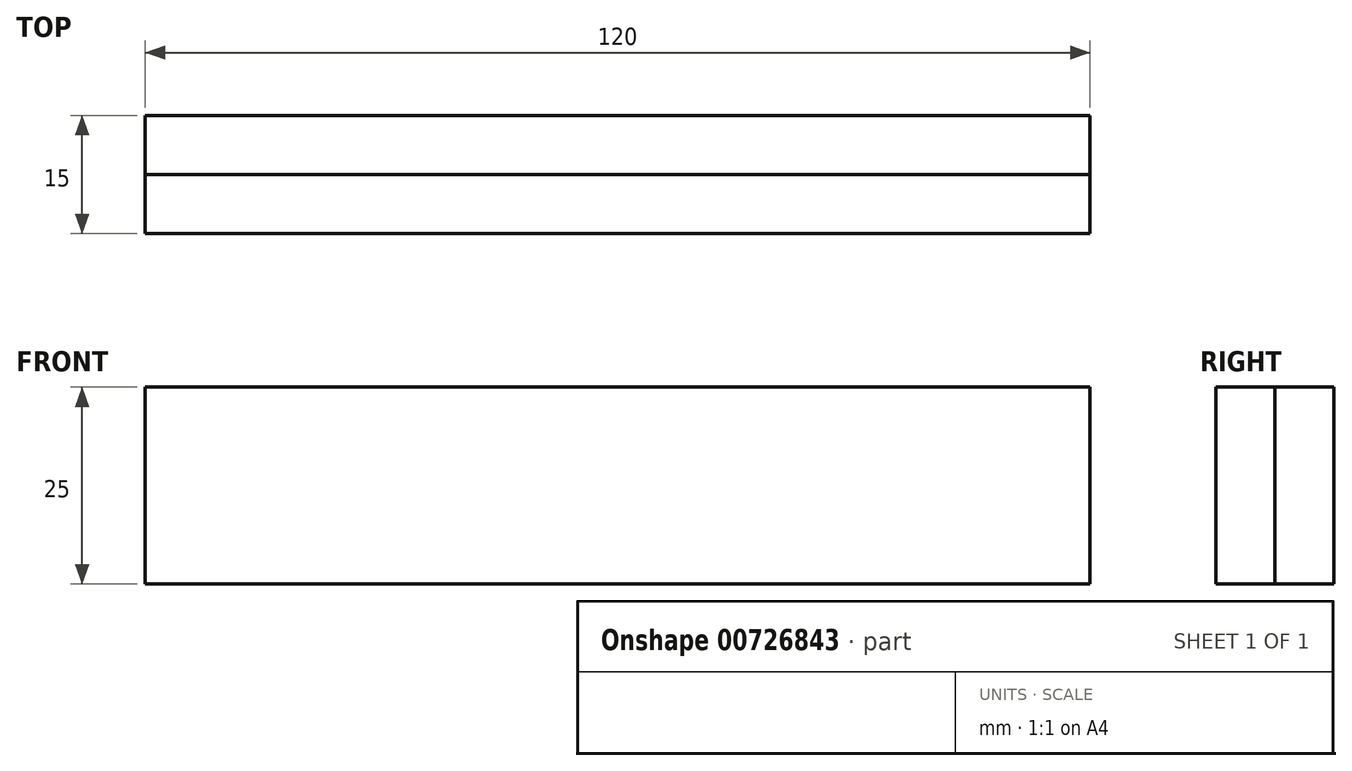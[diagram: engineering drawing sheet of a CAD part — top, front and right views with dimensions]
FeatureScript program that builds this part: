
annotation { "Feature Type Name" : "Feature", "Feature Type Description" : "" }
export const myFeature = defineFeature(function(context is Context, id is Id, definition is map)
    precondition{}
    {
        {
            var Q0;
            Q0=qCreatedBy(makeId("Top.planeOp"),FACE);
            var sketch = newSketch(context, id + "F0", { "sketchPlane" : qUnion([Q0])});
            skLineSegment(sketch, "E0.bottom", {"start": v(-60.51, -1.27) * mm, "end": v(-50.51, -1.27) * mm});
            skLineSegment(sketch, "E0.top", {"start": v(-60.51, -11.27) * mm, "end": v(-50.51, -11.27) * mm});
            skLineSegment(sketch, "E0.left", {"start": v(-60.51, -1.27) * mm, "end": v(-60.51, -11.27) * mm});
            skLineSegment(sketch, "E0.right", {"start": v(-50.51, -1.27) * mm, "end": v(-50.51, -11.27) * mm});
            skCircle(sketch, "E1", {"center": v(-55.51, -6.27) * mm, "radius": 5 * mm});
            skPoint(sketch, "E1.centerSnap0", {"position": v(-55.51, -11.27) * mm});
            skPoint(sketch, "E1.centerSnap1", {"position": v(-60.51, -6.27) * mm});
            skLineSegment(sketch, "E2.bottom", {"start": v(-40.9, 0.93) * mm, "end": v(79.1, 0.93) * mm});
            skLineSegment(sketch, "E2.top", {"start": v(-40.9, -14.07) * mm, "end": v(79.1, -14.07) * mm});
            skLineSegment(sketch, "E2.left", {"start": v(-40.9, 0.93) * mm, "end": v(-40.9, -14.07) * mm});
            skLineSegment(sketch, "E2.right", {"start": v(79.1, 0.93) * mm, "end": v(79.1, -14.07) * mm});
            skLineSegment(sketch, "E3", {"start": v(-40.9, -6.57) * mm, "end": v(79.1, -6.57) * mm});
            skSolve(sketch);
        }
        {
            var Q0;
            {var subQ0=sQuery(id+"F0.wireOp",EDGE,"E0.left");var subQ1=sQuery(id+"F0.wireOp",EDGE,"E0.bottom");var subQ2=makeQuery(id+"F0.imprint","INTERSECT",VERTEX,{"derivedFrom":[subQ1,subQ0]});Q0=makeQuery(id+"F0.imprint","IMPRINT",FACE,{"disambiguationData":[TD([[makeQuery(id+"F0.imprint","IMPRINT",EDGE,{"disambiguationData":[TD([[subQ2,-1.0]])],"derivedFrom":subQ1}),-1.0]])]});}
            var Q1;
            {var subQ0=sQuery(id+"F0.wireOp",EDGE,"E0.right");var subQ1=sQuery(id+"F0.wireOp",EDGE,"E0.bottom");var subQ2=makeQuery(id+"F0.imprint","INTERSECT",VERTEX,{"derivedFrom":[subQ1,subQ0]});Q1=makeQuery(id+"F0.imprint","IMPRINT",FACE,{"disambiguationData":[TD([[makeQuery(id+"F0.imprint","IMPRINT",EDGE,{"disambiguationData":[TD([[subQ2,1.0]])],"derivedFrom":subQ1}),-1.0]])]});}
            var Q2;
            {var subQ0=sQuery(id+"F0.wireOp",EDGE,"E0.left");var subQ1=sQuery(id+"F0.wireOp",EDGE,"E0.top");var subQ2=makeQuery(id+"F0.imprint","INTERSECT",VERTEX,{"derivedFrom":[subQ1,subQ0]});Q2=makeQuery(id+"F0.imprint","IMPRINT",FACE,{"disambiguationData":[TD([[makeQuery(id+"F0.imprint","IMPRINT",EDGE,{"disambiguationData":[TD([[subQ2,-1.0]])],"derivedFrom":subQ1}),1.0]])]});}
            var Q3;
            {var subQ0=sQuery(id+"F0.wireOp",EDGE,"E0.right");var subQ1=sQuery(id+"F0.wireOp",EDGE,"E0.top");var subQ2=makeQuery(id+"F0.imprint","INTERSECT",VERTEX,{"derivedFrom":[subQ1,subQ0]});Q3=makeQuery(id+"F0.imprint","IMPRINT",FACE,{"disambiguationData":[TD([[makeQuery(id+"F0.imprint","IMPRINT",EDGE,{"disambiguationData":[TD([[subQ2,1.0]])],"derivedFrom":subQ1}),1.0]])]});}
            var Q4;
            {var subQ0=sQuery(id+"F0.wireOp",EDGE,"E2.top");Q4=makeQuery(id+"F0.imprint","IMPRINT",FACE,{"disambiguationData":[TD([[makeQuery(id+"F0.imprint","IMPRINT",EDGE,{"derivedFrom":subQ0}),1.0]])]});}
            extrude(context, id + "F1", {"entities" : qUnion([Q0, Q1, Q2, Q3, Q4]), "depth" : 25 * mm, "offsetDistance" : 25 * mm});
        }
        {
            var Q0;
            {var subQ0=sQuery(id+"F0.wireOp",EDGE,"E1");var subQ1=makeQuery(id+"F0.imprint","INTERSECT",VERTEX,{"derivedFrom":[sQuery(id+"F0.wireOp",EDGE,"E0.bottom"),subQ0]});Q0=makeQuery(id+"F0.imprint","IMPRINT",FACE,{"disambiguationData":[TD([[makeQuery(id+"F0.imprint","IMPRINT",EDGE,{"disambiguationData":[TD([[subQ1,1.0]])],"derivedFrom":subQ0}),1.0]])]});}
            var Q1;
            {var subQ0=sQuery(id+"F0.wireOp",EDGE,"E2.bottom");Q1=makeQuery(id+"F0.imprint","IMPRINT",FACE,{"disambiguationData":[TD([[makeQuery(id+"F0.imprint","IMPRINT",EDGE,{"derivedFrom":subQ0}),-1.0]])]});}
            extrude(context, id + "F2", {"entities" : qUnion([Q0, Q1]), "depth" : 25 * mm, "offsetDistance" : 25 * mm});
        }
        {
            var Q0;
            Q0=makeQuery(id+"F1.opExtrude","SWEPT_BODY",BODY,{"disambiguationData":[OSD([sQuery(id+"F0.wireOp",EDGE,"E0.top"),sQuery(id+"F0.wireOp",EDGE,"E0.right"),sQuery(id+"F0.wireOp",EDGE,"E1")])]});
            var Q1;
            Q1=makeQuery(id+"F1.opExtrude","SWEPT_BODY",BODY,{"disambiguationData":[OSD([sQuery(id+"F0.wireOp",EDGE,"E0.bottom"),sQuery(id+"F0.wireOp",EDGE,"E0.right"),sQuery(id+"F0.wireOp",EDGE,"E1")])]});
            var Q2;
            Q2=makeQuery(id+"F1.opExtrude","SWEPT_BODY",BODY,{"disambiguationData":[OSD([sQuery(id+"F0.wireOp",EDGE,"E0.bottom"),sQuery(id+"F0.wireOp",EDGE,"E0.left"),sQuery(id+"F0.wireOp",EDGE,"E1")])]});
            var Q3;
            Q3=makeQuery(id+"F1.opExtrude","SWEPT_BODY",BODY,{"disambiguationData":[OSD([sQuery(id+"F0.wireOp",EDGE,"E0.top"),sQuery(id+"F0.wireOp",EDGE,"E0.left"),sQuery(id+"F0.wireOp",EDGE,"E1")])]});
            var Q4;
            Q4=makeQuery(id+"F2.opExtrude","SWEPT_BODY",BODY,{"disambiguationData":[OSD([sQuery(id+"F0.wireOp",EDGE,"E1")])]});
            deleteBodies(context, id + "F3", {"entities" : qUnion([Q0, Q1, Q2, Q3, Q4])});
        }
    });
